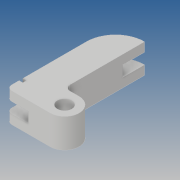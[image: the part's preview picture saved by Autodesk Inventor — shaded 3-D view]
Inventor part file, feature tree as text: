
AUTODESK INVENTOR PART (.ipt)
format: ipt  version: 2019 (Build 230136000, 136)  size: 156,672 bytes
history: native  units: mm
features: sketch x5, extrude x4, fillet x2, projected_geometry x2, hole x1
ambient origin geometry x8: Origin, YZ Plane, XZ Plane, XY Plane, X Axis, Y Axis, Z Axis, Center Point
bodies: Body1 (feature_tree)
feature tree (14):
  extrude  "Extrusion2"  Depth=8.0mm
  extrude  "Extrusion3"  Depth=30.0mm
  extrude  "Extrusion4"  Depth=8.0mm TaperAngle=0.0deg
  hole  "Perçage2"  [1 undecoded]
  fillet  "Congé2"  Radius=6.0mm
  fillet  "Congé3"  Radius=3.0mm
  extrude  "Extrusion5"  Depth=8.0mm
  sketch  "Esquisse3"
  sketch  "Esquisse4"
  projected_geometry  "Boucle projetée1"
  sketch  "Esquisse5"
  sketch  "Esquisse6"
  sketch  "Esquisse7"
  projected_geometry  "Boucle projetée2"
note: 1 required parameter value undecoded (feature->parameter linkage not recoverable at this tier; creation-order binding heuristic only, values carry confidence <= 0.55)
